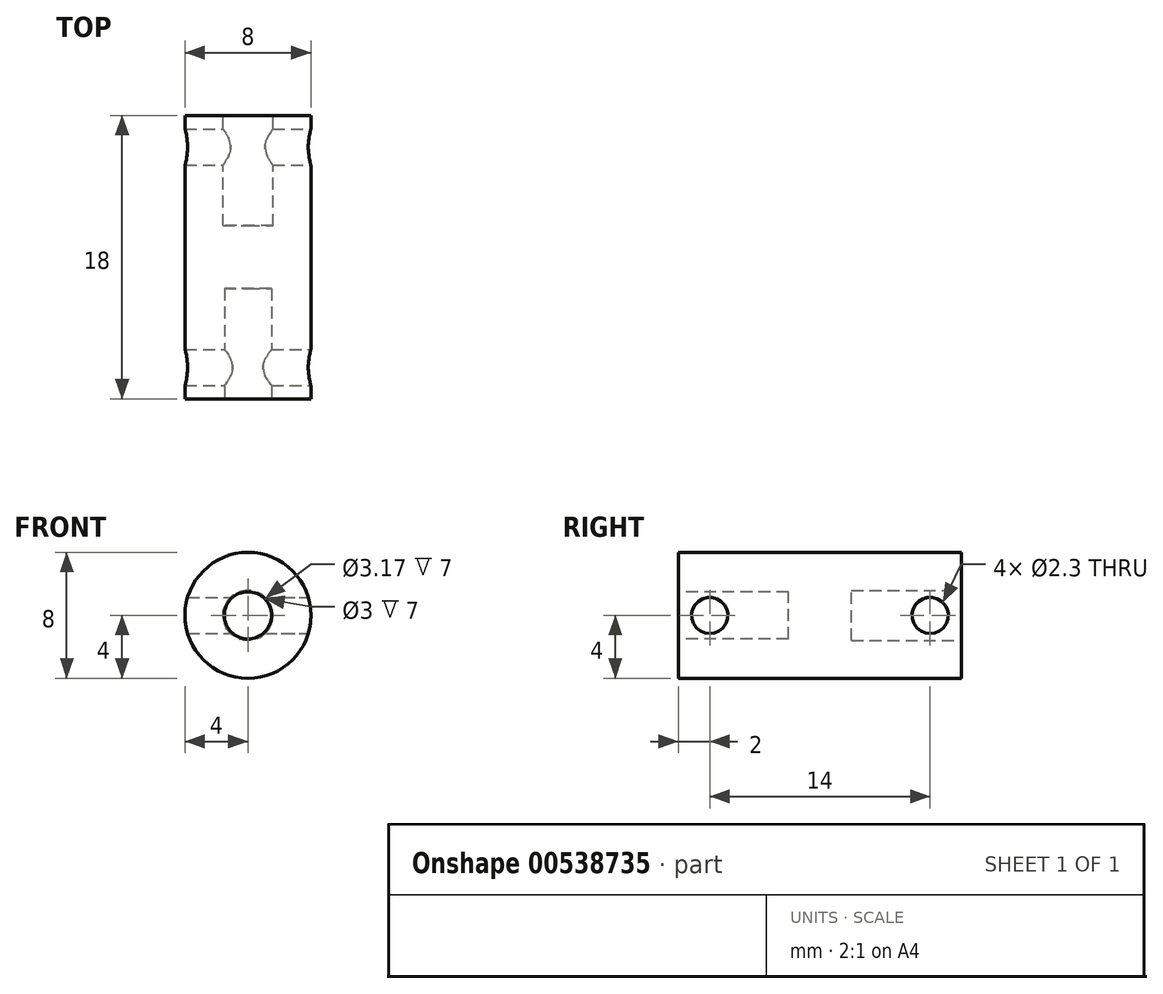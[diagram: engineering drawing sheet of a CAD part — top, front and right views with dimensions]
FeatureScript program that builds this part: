
annotation { "Feature Type Name" : "Feature", "Feature Type Description" : "" }
export const myFeature = defineFeature(function(context is Context, id is Id, definition is map)
    precondition{}
    {
        {
            var Q0;
            Q0=qCreatedBy(makeId("Front.planeOp"),FACE);
            var sketch = newSketch(context, id + "F0", { "sketchPlane" : qUnion([Q0])});
            skCircle(sketch, "E0", {"center": v(0, 0) * mm, "radius": 4 * mm});
            skSolve(sketch);
        }
        {
            var Q0;
            Q0=makeQuery(id+"F0.imprint","IMPRINT",FACE,{"disambiguationData":[TD([[makeQuery(id+"F0.imprint","IMPRINT",EDGE,{"derivedFrom":sQuery(id+"F0.wireOp",EDGE,"E0")}),1.0]])]});
            extrude(context, id + "F1", {"entities" : qUnion([Q0]), "depth" : 18 * mm, "offsetDistance" : 25 * mm});
        }
        {
            var Q0;
            Q0=qCreatedBy(makeId("Right.planeOp"),FACE);
            var sketch = newSketch(context, id + "F2", { "sketchPlane" : qUnion([Q0])});
            skCircle(sketch, "E1", {"center": v(-16, 0) * mm, "radius": 1.15 * mm});
            skCircle(sketch, "E2", {"center": v(-2, 0) * mm, "radius": 1.15 * mm});
            skSolve(sketch);
        }
        {
            var Q0;
            Q0 = qSketchRegion(id + "F2", true);
            extrude(context, id + "F3", {"entities" : qUnion([Q0]), "operationType" : NewBodyOperationType.REMOVE, "endBound" : BoundingType.THROUGH_ALL, "oppositeDirection" : true, "depth" : 25 * mm, "offsetDistance" : 25 * mm, "hasSecondDirection" : true, "secondDirectionBound" : SecondDirectionBoundingType.THROUGH_ALL, "secondDirectionOppositeDirection" : false, "secondDirectionDepth" : 25 * mm});
        }
        {
            var Q0;
            Q0=qCreatedBy(makeId("Front.planeOp"),FACE);
            var sketch = newSketch(context, id + "F4", { "sketchPlane" : qUnion([Q0])});
            skCircle(sketch, "E3", {"center": v(0, 0) * mm, "radius": 1.58 * mm});
            skSolve(sketch);
        }
        {
            var Q0;
            Q0=makeQuery(id+"F4.imprint","IMPRINT",FACE,{"disambiguationData":[TD([[makeQuery(id+"F4.imprint","IMPRINT",EDGE,{"derivedFrom":sQuery(id+"F4.wireOp",EDGE,"E3")}),1.0]])]});
            extrude(context, id + "F5", {"entities" : qUnion([Q0]), "operationType" : NewBodyOperationType.REMOVE, "depth" : 7 * mm, "offsetDistance" : 25 * mm});
        }
        {
            var Q0;
            Q0=qCreatedBy(makeId("Front.planeOp"),FACE);
            cPlane(context, id + "F6", {"entities" : qUnion([Q0]), "cplaneType" : CPlaneType.OFFSET, "offset" : 18 * mm, "width" : 150 * mm, "height" : 150 * mm});
        }
        {
            var Q0;
            Q0=qCreatedBy(id+"F6.planeOp",FACE);
            var sketch = newSketch(context, id + "F7", { "sketchPlane" : qUnion([Q0])});
            skCircle(sketch, "E4", {"center": v(0, 0) * mm, "radius": 1.5 * mm});
            skSolve(sketch);
        }
        {
            var Q0;
            Q0=makeQuery(id+"F7.imprint","IMPRINT",FACE,{"disambiguationData":[TD([[makeQuery(id+"F7.imprint","IMPRINT",EDGE,{"derivedFrom":sQuery(id+"F7.wireOp",EDGE,"E4")}),1.0]])]});
            extrude(context, id + "F8", {"entities" : qUnion([Q0]), "operationType" : NewBodyOperationType.REMOVE, "oppositeDirection" : true, "depth" : 7 * mm, "offsetDistance" : 25 * mm});
        }
    });
